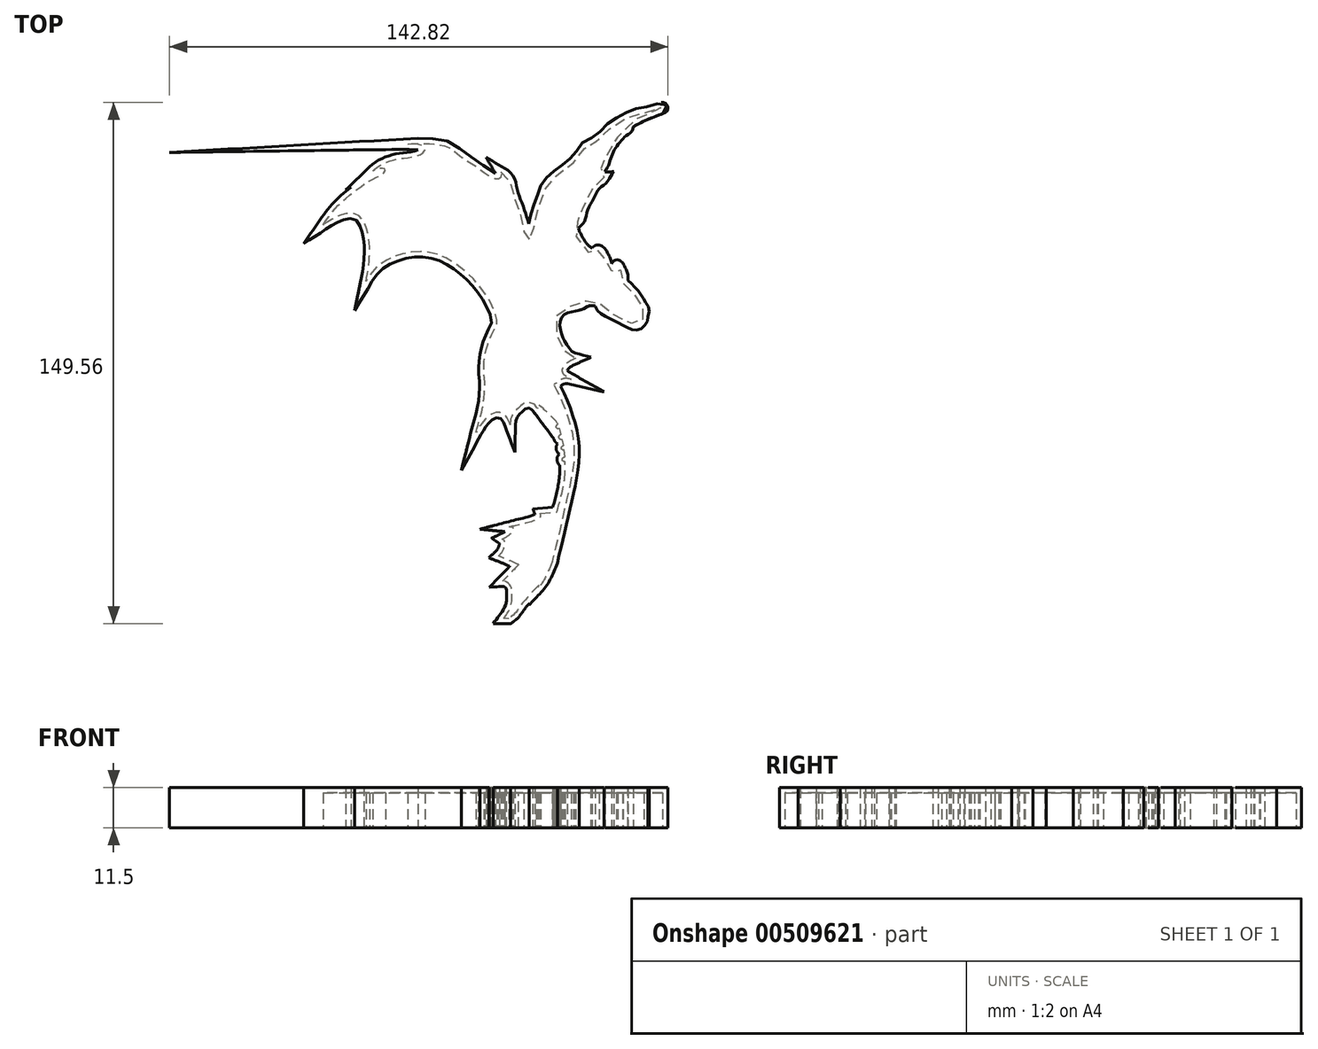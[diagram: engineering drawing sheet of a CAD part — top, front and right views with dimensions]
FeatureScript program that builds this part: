
annotation { "Feature Type Name" : "Feature", "Feature Type Description" : "" }
export const myFeature = defineFeature(function(context is Context, id is Id, definition is map)
    precondition{}
    {
        {
            var Q0;
            Q0=qCreatedBy(makeId("Top.planeOp"),FACE);
            var sketch = newSketch(context, id + "F0", { "sketchPlane" : qUnion([Q0])});
            skFitSpline(sketch, "E0", {"points": [v(-6.63, -72.94) * mm, v(-8.13, -72.91) * mm], "startDerivative": vector(-1.5, 0.03) * mm, "endDerivative": vector(-1.5, 0.03) * mm});
            skFitSpline(sketch, "E1", {"points": [v(6.3, -5.91) * mm, v(8.4, -10.1) * mm, v(10.77, -16.63) * mm, v(11.89, -21.8) * mm, v(11.94, -28.58) * mm, v(9.84, -39.3) * mm, v(7.53, -49.66) * mm, v(6.03, -55.58) * mm, v(5.84, -56.64) * mm], "startDerivative": vector(19, -35.26) * mm, "endDerivative": vector(-2.34, -16.37) * mm});
            skFitSpline(sketch, "E2", {"points": [v(5.84, -56.64) * mm, v(4.68, -59.43) * mm, v(2.97, -62.67) * mm, v(1.91, -63.96) * mm], "startDerivative": vector(-3.02, -7.55) * mm, "endDerivative": vector(-3.9, -4.18) * mm});
            skFitSpline(sketch, "E3", {"points": [v(1.91, -63.96) * mm, v(2.07, -63.29) * mm], "startDerivative": vector(0.16, 0.68) * mm, "endDerivative": vector(0.16, 0.68) * mm});
            skFitSpline(sketch, "E4", {"points": [v(2.07, -63.29) * mm, v(-0.9, -66.46) * mm, v(-3.77, -69.97) * mm, v(-6.63, -72.94) * mm], "startDerivative": vector(-9.02, -9.21) * mm, "endDerivative": vector(-18.52, -13.48) * mm});
            skFitSpline(sketch, "E5", {"points": [v(-8.13, -72.91) * mm, v(-6.56, -70.55) * mm, v(-5.8, -68.14) * mm, v(-5.75, -65.57) * mm, v(-6.15, -63.47) * mm, v(-8.39, -62.2) * mm], "startDerivative": vector(8.12, 10.93) * mm, "endDerivative": vector(-14.62, -0.93) * mm});
            skFitSpline(sketch, "E6", {"points": [v(-8.39, -62.2) * mm, v(-5.96, -59.7) * mm, v(-3.77, -57.43) * mm], "startDerivative": vector(4.8, 4.96) * mm, "endDerivative": vector(4.44, 4.6) * mm});
            skFitSpline(sketch, "E7", {"points": [v(-3.77, -57.43) * mm, v(-6.76, -56.11) * mm, v(-9.59, -54.97) * mm], "startDerivative": vector(-5.9, 2.66) * mm, "endDerivative": vector(-5.72, 2.27) * mm});
            skFitSpline(sketch, "E8", {"points": [v(-9.59, -54.97) * mm, v(-8.5, -53.74) * mm, v(-7.83, -51.83) * mm, v(-7.9, -50.64) * mm, v(-8.5, -50.1) * mm], "startDerivative": vector(4.3, 3.97) * mm, "endDerivative": vector(-3.66, 2.4) * mm});
            skFitSpline(sketch, "E9", {"points": [v(-8.5, -50.1) * mm, v(-7.12, -49.4) * mm, v(-6.04, -48.5) * mm, v(-5.37, -47.5) * mm, v(-5.46, -46.87) * mm, v(-6.43, -46.61) * mm], "startDerivative": vector(6.15, 2.78) * mm, "endDerivative": vector(-6.28, 0.6) * mm});
            skFitSpline(sketch, "E10", {"points": [v(-6.43, -46.61) * mm, v(-4.24, -46.06) * mm, v(-1.44, -45.4) * mm, v(1.37, -44.49) * mm, v(2.52, -43.73) * mm, v(2.38, -42.78) * mm], "startDerivative": vector(10, 2.66) * mm, "endDerivative": vector(-2.75, 7.4) * mm});
            skFitSpline(sketch, "E11", {"points": [v(2.38, -42.78) * mm, v(7.15, -42.38) * mm], "startDerivative": vector(4.78, 0.4) * mm, "endDerivative": vector(4.78, 0.4) * mm});
            skFitSpline(sketch, "E12", {"points": [v(7.15, -42.38) * mm, v(8.3, -38.16) * mm, v(9.35, -32.8) * mm, v(9.53, -27.97) * mm], "startDerivative": vector(3.66, 12.87) * mm, "endDerivative": vector(-0.05, 14.29) * mm});
            skFitSpline(sketch, "E13", {"points": [v(9.53, -27.97) * mm, v(9.45, -26.5) * mm], "startDerivative": vector(-3.33, 0.42) * mm, "endDerivative": vector(3.1, 1.19) * mm});
            skFitSpline(sketch, "E14", {"points": [v(9.45, -26.5) * mm, v(9.3, -24.62) * mm], "startDerivative": vector(-0.15, 1.88) * mm, "endDerivative": vector(-0.15, 1.88) * mm});
            skFitSpline(sketch, "E15", {"points": [v(9.3, -24.62) * mm, v(9.09, -23.27) * mm], "startDerivative": vector(-3.28, -0.18) * mm, "endDerivative": vector(2.8, 0.92) * mm});
            skFitSpline(sketch, "E16", {"points": [v(9.09, -23.27) * mm, v(8.78, -21.64) * mm], "startDerivative": vector(-0.3, 1.63) * mm, "endDerivative": vector(-0.3, 1.63) * mm});
            skFitSpline(sketch, "E17", {"points": [v(8.78, -21.64) * mm, v(8.38, -20.04) * mm], "startDerivative": vector(-2.88, -0.55) * mm, "endDerivative": vector(3.46, 1.66) * mm});
            skFitSpline(sketch, "E18", {"points": [v(8.38, -20.04) * mm, v(7.97, -18.54) * mm], "startDerivative": vector(-0.41, 1.5) * mm, "endDerivative": vector(-0.41, 1.5) * mm});
            skFitSpline(sketch, "E19", {"points": [v(7.97, -18.54) * mm, v(7.43, -17.06) * mm], "startDerivative": vector(-2.48, -0.58) * mm, "endDerivative": vector(2.54, 2.75) * mm});
            skFitSpline(sketch, "E20", {"points": [v(7.43, -17.06) * mm, v(6.44, -15.76) * mm, v(4.5, -13.96) * mm, v(2.43, -12.1) * mm, v(1.7, -12.72) * mm], "startDerivative": vector(-3.82, 5.71) * mm, "endDerivative": vector(15.54, -29) * mm});
            skFitSpline(sketch, "E21", {"points": [v(1.7, -12.72) * mm, v(0.76, -11.63) * mm, v(-0.38, -11.07) * mm, v(-2.34, -11.34) * mm, v(-4.05, -12.72) * mm, v(-5.87, -15.09) * mm, v(-6.22, -17.36) * mm], "startDerivative": vector(-6.26, 8.35) * mm, "endDerivative": vector(-0.25, -12.77) * mm});
            skFitSpline(sketch, "E22", {"points": [v(-6.22, -17.36) * mm, v(-7.15, -15.33) * mm, v(-8.68, -14) * mm, v(-11.3, -14.16) * mm, v(-14.52, -17.18) * mm, v(-15.97, -19.55) * mm], "startDerivative": vector(-4.44, 11.86) * mm, "endDerivative": vector(-6.05, -11.1) * mm});
            skFitSpline(sketch, "E23", {"points": [v(-15.97, -19.55) * mm, v(-15.3, -17) * mm, v(-14.28, -13.41) * mm, v(-13.74, -9.83) * mm, v(-13.53, -5.24) * mm, v(-13.77, -0.68) * mm, v(-12.76, 5.38) * mm, v(-11.28, 9.1) * mm, v(-10.03, 11.44) * mm], "startDerivative": vector(5.85, 23.68) * mm, "endDerivative": vector(12.07, 21.84) * mm});
            skFitSpline(sketch, "E24", {"points": [v(-10.03, 11.44) * mm, v(-10.12, 13.3) * mm, v(-11.28, 16.5) * mm, v(-13.27, 20) * mm, v(-16.33, 24) * mm, v(-21.18, 28.28) * mm, v(-26.74, 31.4) * mm, v(-33.63, 32.24) * mm, v(-40.2, 30.55) * mm, v(-44.74, 27.68) * mm, v(-47.54, 23.78) * mm], "startDerivative": vector(0.98, 28.48) * mm, "endDerivative": vector(-25.3, -42.15) * mm});
            skFitSpline(sketch, "E25", {"points": [v(-47.54, 23.78) * mm, v(-46.9, 27.29) * mm, v(-46.52, 32.27) * mm, v(-46.93, 37.2) * mm, v(-49.55, 42.58) * mm, v(-54.2, 42.96) * mm, v(-59.9, 39.95) * mm], "startDerivative": vector(4.9, 23.7) * mm, "endDerivative": vector(-29.76, -19.32) * mm});
            skFitSpline(sketch, "E26", {"points": [v(-59.9, 39.95) * mm, v(-56.75, 44.2) * mm, v(-53.13, 47.8) * mm, v(-49.16, 50.86) * mm, v(-45.82, 53.02) * mm, v(-42.36, 54.9) * mm, v(-42.05, 55.9) * mm, v(-43.23, 56.23) * mm, v(-45.6, 55.38) * mm], "startDerivative": vector(19.08, 27.58) * mm, "endDerivative": vector(-22.27, -10.65) * mm});
            skFitSpline(sketch, "E27", {"points": [v(-45.6, 55.38) * mm, v(-43.7, 56.93) * mm, v(-39.81, 58.57) * mm, v(-36.34, 59.17) * mm, v(-31.73, 60.31) * mm, v(-30.6, 61.9) * mm, v(-32.17, 62.92) * mm, v(-35.57, 63.15) * mm], "startDerivative": vector(12.82, 12.33) * mm, "endDerivative": vector(-23.6, -0.31) * mm});
            skFitSpline(sketch, "E28", {"points": [v(-35.57, 63.15) * mm, v(-31.22, 63.31) * mm, v(-27.06, 63.05) * mm, v(-23.72, 62.12) * mm, v(-20.34, 59.61) * mm, v(-16.46, 57.05) * mm, v(-13.44, 54.8) * mm, v(-11.1, 53.44) * mm, v(-9.37, 53.35) * mm, v(-8.61, 54.24) * mm, v(-8.94, 55.18) * mm], "startDerivative": vector(35.8, 2.05) * mm, "endDerivative": vector(-9.48, 16.04) * mm});
            skFitSpline(sketch, "E29", {"points": [v(-8.94, 55.18) * mm, v(-7.2, 53.98) * mm, v(-6.18, 52.16) * mm, v(-5.34, 48.65) * mm, v(-3.87, 44.71) * mm, v(-3.07, 42.27) * mm, v(-2.3, 39.78) * mm, v(-2.21, 37.37) * mm, v(-1.98, 37.01) * mm, v(-0.85, 35.81) * mm, v(-0.45, 35.7) * mm, v(0.16, 36.61) * mm, v(0.57, 39.77) * mm, v(1.68, 44.34) * mm, v(3.37, 48.84) * mm, v(4.24, 51.23) * mm, v(7.38, 54.3) * mm, v(11.37, 57.35) * mm, v(14.38, 60.75) * mm, v(15.47, 62.38) * mm, v(17.1, 63.37) * mm, v(19.4, 64.51) * mm, v(22.1, 67.36) * mm, v(25.7, 69.77) * mm, v(29.73, 71.71) * mm, v(33.4, 72.38) * mm, v(36.33, 73.31) * mm, v(37.29, 73.62) * mm, v(37.47, 73.52) * mm, v(37.08, 73.3) * mm, v(33.93, 72.14) * mm, v(29.73, 70.23) * mm, v(27.8, 68.99) * mm, v(27.56, 68.34) * mm, v(27.45, 67.71) * mm, v(26.37, 66.94) * mm, v(22.37, 62.22) * mm, v(20.96, 58.77) * mm, v(20.57, 57.63) * mm, v(19.67, 55.9) * mm, v(19.4, 53.92) * mm, v(20.66, 53.64) * mm], "startDerivative": vector(82.71, -47.31) * mm, "endDerivative": vector(88.06, 2.75) * mm});
            skFitSpline(sketch, "E30", {"points": [v(20.66, 53.64) * mm, v(20.02, 52.86) * mm, v(18.02, 51.26) * mm, v(16.3, 48.09) * mm, v(14.8, 45.35) * mm, v(14.16, 43.24) * mm, v(13.51, 41.36) * mm, v(12.03, 39.7) * mm, v(12.09, 37.99) * mm, v(13.56, 35.12) * mm, v(15.23, 32.9) * mm, v(17.74, 31.43) * mm, v(18.44, 31.64) * mm, v(18.54, 32.56) * mm, v(18.83, 32.7) * mm, v(19.7, 32.26) * mm, v(20.74, 30.51) * mm, v(21.26, 29.3) * mm, v(21.6, 27.68) * mm, v(22.3, 27.09) * mm, v(23.44, 26.43) * mm, v(24.07, 25.7) * mm, v(24.48, 25.77) * mm, v(24.38, 27.58) * mm, v(24.26, 28.39) * mm, v(24.65, 28.35) * mm, v(25.54, 26.75) * mm, v(26.08, 25.37) * mm, v(26.05, 23.63) * mm, v(26.94, 22.6) * mm, v(28.21, 21.39) * mm, v(29.66, 19.64) * mm, v(30.78, 17.98) * mm, v(31.6, 16.47) * mm, v(32.12, 15.45) * mm, v(31.76, 13.82) * mm, v(31.7, 12.93) * mm, v(31, 11.87) * mm, v(29.83, 11.3) * mm, v(27.7, 12.06) * mm, v(24.44, 13.7) * mm, v(21.09, 15.46) * mm, v(19.72, 16.71) * mm, v(19.42, 17.46) * mm, v(18.38, 18.17) * mm, v(15.84, 18.23) * mm, v(14.75, 17.6) * mm, v(12, 16.68) * mm, v(9.46, 16.12) * mm, v(7.65, 14.83) * mm, v(6.6, 12.27) * mm, v(6.82, 9.16) * mm, v(7.83, 6.27) * mm, v(8.87, 4.66) * mm, v(9.93, 3.19) * mm, v(10.86, 2.3) * mm, v(12.55, 1.68) * mm], "startDerivative": vector(-35.87, -57.25) * mm, "endDerivative": vector(102.8, -28.82) * mm});
            skFitSpline(sketch, "E31", {"points": [v(12.55, 1.68) * mm, v(10.47, 0.63) * mm, v(8.99, -0.73) * mm, v(8.76, -2.31) * mm, v(11.25, -4.27) * mm], "startDerivative": vector(-8.44, -3.8) * mm, "endDerivative": vector(10.91, -6.2) * mm});
            skFitSpline(sketch, "E32", {"points": [v(11.25, -4.27) * mm, v(8.97, -4.13) * mm, v(6.3, -5.91) * mm], "startDerivative": vector(-5, 1.1) * mm, "endDerivative": vector(-4.9, -4.25) * mm});
            skSolve(sketch);
        }
        {
            var Q0;
            Q0=makeQuery(id+"F0.imprint","IMPRINT",FACE,{"disambiguationData":[TD([[makeQuery(id+"F0.imprint","IMPRINT",EDGE,{"derivedFrom":sQuery(id+"F0.wireOp",EDGE,"E0")}),-1.0]])]});
            extrude(context, id + "F1", {"entities" : qUnion([Q0]), "depth" : 10 * mm, "offsetDistance" : 25 * mm});
        }
        {
            var Q0;
            Q0=makeQuery(id+"F1.opExtrude","CAP_FACE",FACE,{"disambiguationData":[OSD([sQuery(id+"F0.wireOp",EDGE,"E0"),sQuery(id+"F0.wireOp",EDGE,"E1"),sQuery(id+"F0.wireOp",EDGE,"E2"),sQuery(id+"F0.wireOp",EDGE,"E3"),sQuery(id+"F0.wireOp",EDGE,"E4"),sQuery(id+"F0.wireOp",EDGE,"E5"),sQuery(id+"F0.wireOp",EDGE,"E6"),sQuery(id+"F0.wireOp",EDGE,"E7"),sQuery(id+"F0.wireOp",EDGE,"E8"),sQuery(id+"F0.wireOp",EDGE,"E9"),sQuery(id+"F0.wireOp",EDGE,"E10"),sQuery(id+"F0.wireOp",EDGE,"E11"),sQuery(id+"F0.wireOp",EDGE,"E12"),sQuery(id+"F0.wireOp",EDGE,"E13"),sQuery(id+"F0.wireOp",EDGE,"E14"),sQuery(id+"F0.wireOp",EDGE,"E15"),sQuery(id+"F0.wireOp",EDGE,"E16"),sQuery(id+"F0.wireOp",EDGE,"E17"),sQuery(id+"F0.wireOp",EDGE,"E18"),sQuery(id+"F0.wireOp",EDGE,"E19"),sQuery(id+"F0.wireOp",EDGE,"E20"),sQuery(id+"F0.wireOp",EDGE,"E21"),sQuery(id+"F0.wireOp",EDGE,"E22"),sQuery(id+"F0.wireOp",EDGE,"E23"),sQuery(id+"F0.wireOp",EDGE,"E24"),sQuery(id+"F0.wireOp",EDGE,"E25"),sQuery(id+"F0.wireOp",EDGE,"E26"),sQuery(id+"F0.wireOp",EDGE,"E27"),sQuery(id+"F0.wireOp",EDGE,"E28"),sQuery(id+"F0.wireOp",EDGE,"E29"),sQuery(id+"F0.wireOp",EDGE,"E30"),sQuery(id+"F0.wireOp",EDGE,"E31"),sQuery(id+"F0.wireOp",EDGE,"E32")])],"isStart":true});
            shell(context, id + "F2", {"entities" : qUnion([Q0]), "thickness" : 1.5 * mm, "oppositeDirection" : true});
        }
    });
